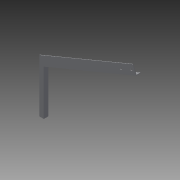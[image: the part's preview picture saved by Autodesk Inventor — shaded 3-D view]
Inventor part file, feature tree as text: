
AUTODESK INVENTOR PART (.ipt)
format: ipt  version: 2013 (Build 170138000, 138)  size: 182,272 bytes
history: native  units: in
note: dims shown in document units (in); Inventor stores cm internally (conversion verified against a paired STEP export)
features: extrude x6, sketch x6, plane x1
ambient origin geometry x8: Origin, YZ Plane, XZ Plane, XY Plane, X Axis, Y Axis, Z Axis, Center Point
bodies: Solid1 (feature_tree)
feature tree (13):
  plane  "Work Plane1"
  extrude  "Extrusion1"  Depth=19.0in
  extrude  "Extrusion2"  TaperAngle=90.0deg  [1 undecoded]
  extrude  "Extrusion3"  TaperAngle=90.0deg  [1 undecoded]
  extrude  "Extrusion4"  TaperAngle=90.0deg  [1 undecoded]
  extrude  "Extrusion5"  TaperAngle=90.0deg  [1 undecoded]
  extrude  "Extrusion6"  Depth=7.0in
  sketch  "Sketch1"  dims[d0=2.5in d1=19.0in]
  sketch  "Sketch2"  dims[d2=3.0in d3=90.0deg]
  sketch  "Sketch4"  dims[d4=5.0in d5=90.0deg]
  sketch  "Sketch5"  dims[d6=4.0in d7=90.0deg]
  sketch  "Sketch6"  dims[d8=53.0in d9=90.0deg]
  sketch  "Sketch7"  dims[d10=21.0in d11=7.0in d12=0.5in d14=2.5in d15=0.5in d16=0.75in d17=22.5deg d18=0.5in d19=90.0deg d20=90.0deg d21=0.5in d22=112.5deg d23=23.2731in d24=90.0deg d25=10.0in d26=90.0deg d27=1.0in d28=90.0deg d29=90.0deg d30=1.0in d31=0.0in d32=22.5deg d33=1.0in d34=112.5deg d35=2.0in d36=0.0in d39=1.0in d40=2.0in d42=157.5deg d43=1.0in d44=0.0in d59=1.0in d60=0.0in d61=0.125in d62=180.0deg d63=0.125in d64=112.5deg d65=90.0deg d66=0.875in d67=0.0in d68=1.875in d69=0.0in d70=0.875in d71=0.0in]
note: 4 required parameter values undecoded (feature->parameter linkage not recoverable at this tier; creation-order binding heuristic only, values carry confidence <= 0.55)
